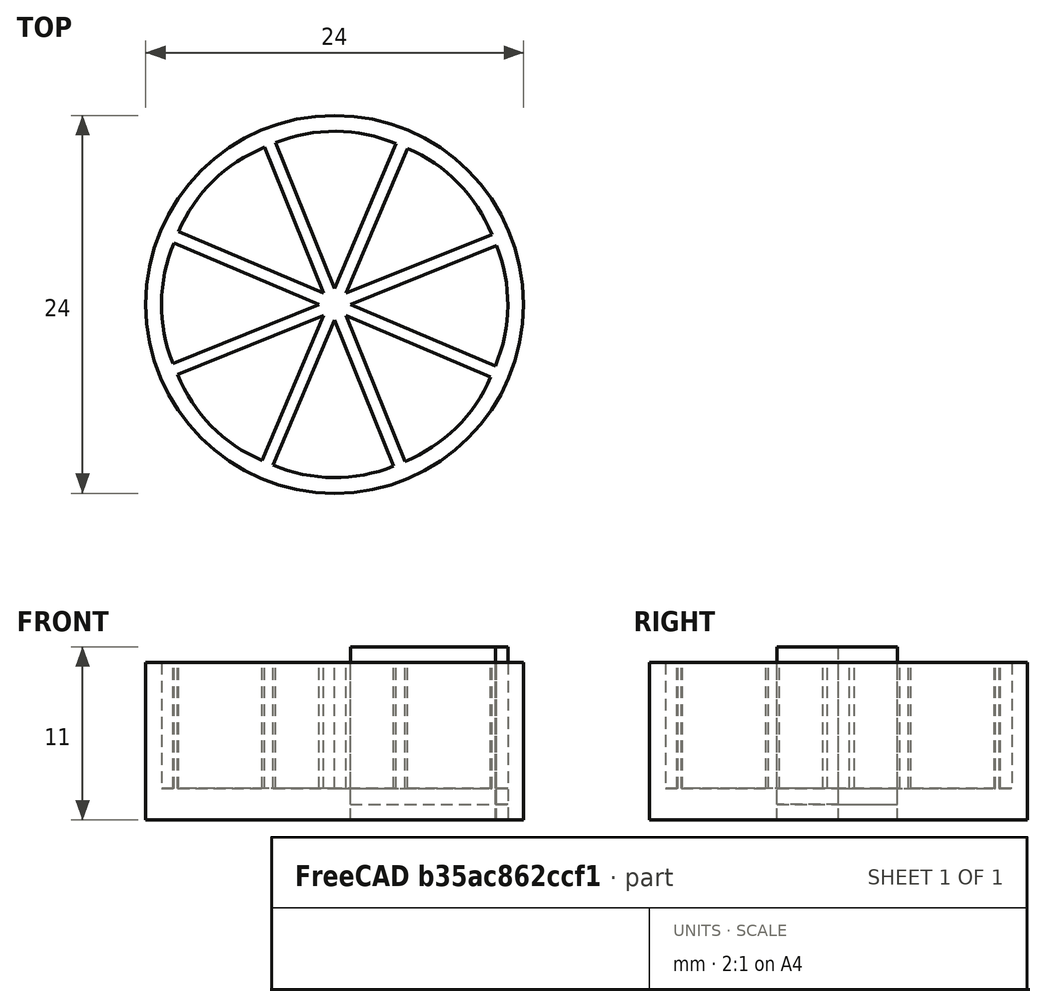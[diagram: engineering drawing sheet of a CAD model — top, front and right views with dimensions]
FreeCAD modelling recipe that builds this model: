
FCSTD DOCUMENT  (FreeCAD 1.0R39319 (Git))
Label: ojt1_t11r02_trivial
License: All rights reserved
LicenseURL: https://en.wikipedia.org/wiki/All_rights_reserved
objects: Part::Cylinder×5, Part::Cut×3, Part::FeaturePython×1
note: 8 computed .brp shape members not serialized (recipe doc carries the construction recipe); baked Part::Feature solids carry a one-line shape summary decoded from their .brp

FEATURE [Part::Cylinder] Cylinder  label="Cilindre"
  Angle = 360
  AttacherType = Attacher::AttachEngine3D
  FirstAngle = 0
  Height = 10
  Radius = 10
  SecondAngle = 0
FEATURE [Part::Cylinder] Cylinder001  label="Cilindre001"
  Angle = 315
  AttacherType = Attacher::AttachEngine3D
  FirstAngle = 0
  Height = 10
  Radius = 10
  SecondAngle = 0
FEATURE [Part::Cut] Cut
  Base = -> Cylinder
  Placement = pos=(1,0,0) rot=(0,0,1;0.383972rad)
  Tool = -> Cylinder001
FEATURE [Part::FeaturePython] Array  # Draft array (typed FeaturePython)
  AlwaysSyncPlacement = false
  Angle = 360
  ArrayType = 1
  Axis = (0,0,1)
  Base = -> Cut
  Center = (0,0,0)
  Count = 8
  ExpandArray = false
  Fuse = false
  IntervalAxis = (0,0,0)
  IntervalX = (100,0,0)
  IntervalY = (0,100,0)
  IntervalZ = (0,0,100)
  NumberCircles = 3
  NumberPolar = 8
  NumberX = 2
  NumberY = 2
  NumberZ = 1
  Placement = pos=(0,0,2) rot=(0,0,1;0rad)
  PlacementList = 8 placements: [(1,0,0),(0.707107,0.707107,0),(0,1,0),(-0.707107,0.707107,0),(-1,1.22465e-16,0),(-0.707107,-0.707107,0),(-2.22045e-16,-1,0),(0.707107,-0.707107,0)]
  RadialDistance = 50
  ScaleList = (8) [(1,1,1),(1,1,1),(1,1,1),(1,1,1),(1,1,1),(1,1,1),(1,1,1),(1,1,1)]
  Symmetry = 1
  TangentialDistance = 25
FEATURE [Part::Cylinder] Cylinder002  label="Cilindre002"
  Angle = 360
  AttacherType = Attacher::AttachEngine3D
  FirstAngle = 0
  Height = 10
  Radius = 12
  SecondAngle = 0
FEATURE [Part::Cut] Cut001
  Base = -> Cylinder002
  Tool = -> Array
FEATURE [Part::Cylinder] Cylinder003  label="Cilindre003"
  Angle = 360
  AttacherType = Attacher::AttachEngine3D
  FirstAngle = 0
  Height = 10
  Radius = 10
  SecondAngle = 0
FEATURE [Part::Cylinder] Cylinder004  label="Cilindre004"
  Angle = 315
  AttacherType = Attacher::AttachEngine3D
  FirstAngle = 0
  Height = 10
  Radius = 10
  SecondAngle = 0
FEATURE [Part::Cut] Cut002
  Base = -> Cylinder003
  Placement = pos=(1,0,1) rot=(0,0,1;0.383972rad)
  Tool = -> Cylinder004
